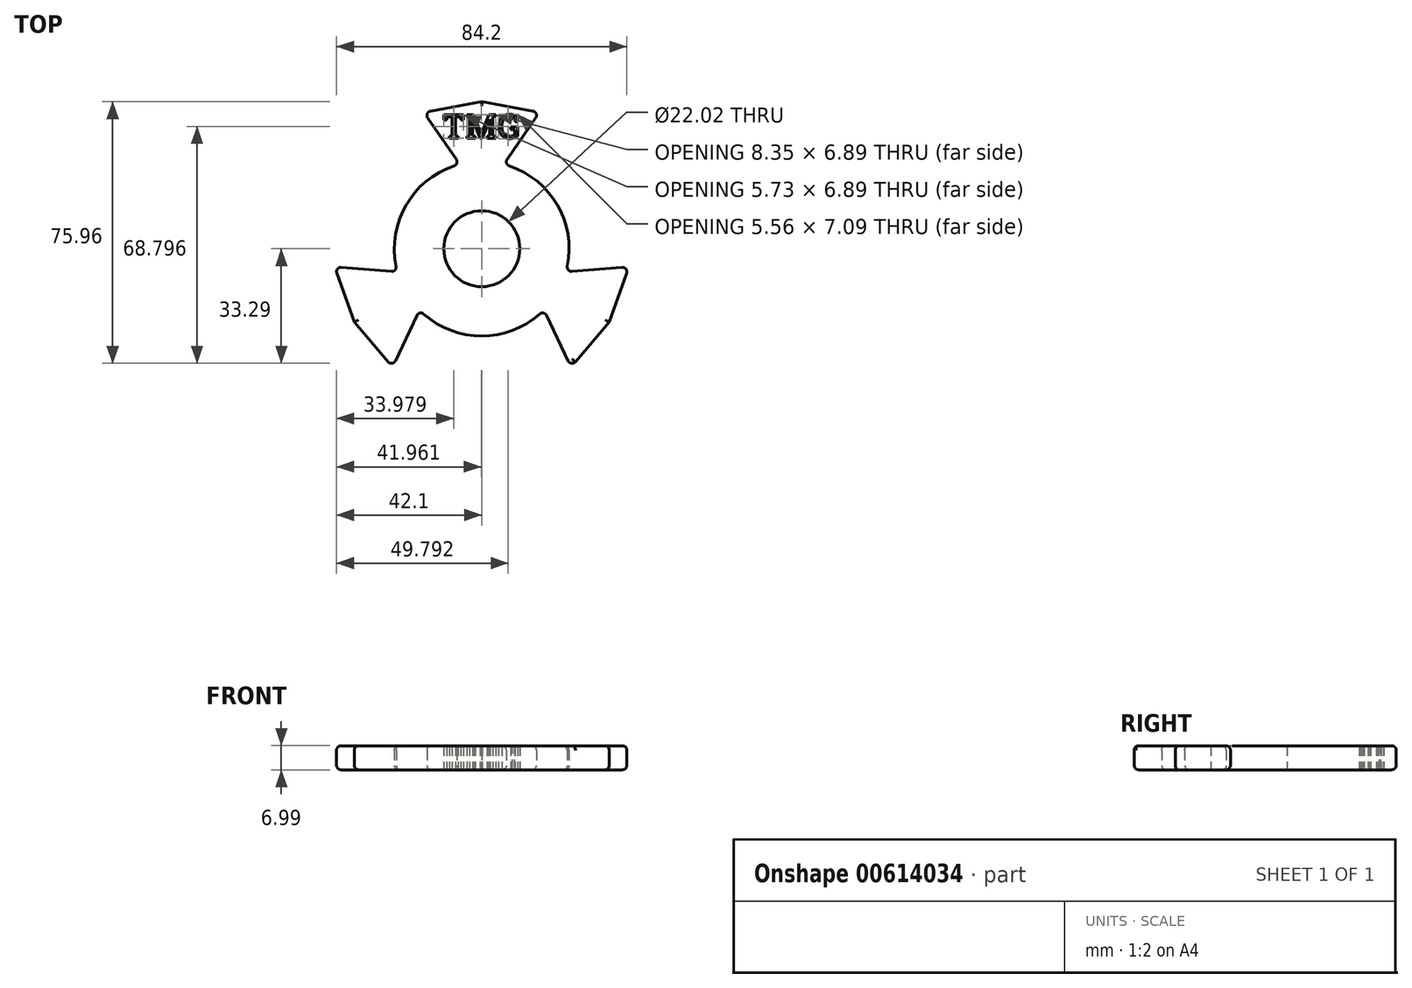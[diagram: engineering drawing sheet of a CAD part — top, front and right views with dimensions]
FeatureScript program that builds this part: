
annotation { "Feature Type Name" : "Feature", "Feature Type Description" : "" }
export const myFeature = defineFeature(function(context is Context, id is Id, definition is map)
    precondition{}
    {
        {
            var Q0;
            Q0=qCreatedBy(makeId("Top.planeOp"),FACE);
            var sketch = newSketch(context, id + "F0", { "sketchPlane" : qUnion([Q0])});
            skCircle(sketch, "E0", {"center": v(0, 0) * mm, "radius": 11.01 * mm});
            skCircle(sketch, "E1", {"center": v(0, 0) * mm, "radius": 25.34 * mm});
            skLineSegment(sketch, "E2", {"start": v(6.38, 24.52) * mm, "end": v(16.79, 39.6) * mm});
            skLineSegment(sketch, "E3", {"start": v(16.79, 39.6) * mm, "end": v(0, 42.67) * mm});
            skLineSegment(sketch, "E4", {"start": v(0, 42.67) * mm, "end": v(-16.79, 39.6) * mm});
            skLineSegment(sketch, "E5", {"start": v(-16.79, 39.6) * mm, "end": v(-6.38, 24.52) * mm});
            skLineSegment(sketch, "E6", {"start": v(-24.43, -6.73) * mm, "end": v(-42.68, -5.26) * mm});
            skLineSegment(sketch, "E7", {"start": v(-42.68, -5.26) * mm, "end": v(-36.96, -21.34) * mm});
            skLineSegment(sketch, "E8", {"start": v(-36.96, -21.34) * mm, "end": v(-25.9, -34.34) * mm});
            skLineSegment(sketch, "E9", {"start": v(-25.9, -34.34) * mm, "end": v(-18.04, -17.79) * mm});
            skLineSegment(sketch, "E10", {"start": v(18.04, -17.79) * mm, "end": v(25.9, -34.34) * mm});
            skLineSegment(sketch, "E11", {"start": v(25.9, -34.34) * mm, "end": v(36.96, -21.34) * mm});
            skLineSegment(sketch, "E12", {"start": v(36.96, -21.34) * mm, "end": v(42.68, -5.26) * mm});
            skLineSegment(sketch, "E13", {"start": v(42.68, -5.26) * mm, "end": v(24.43, -6.73) * mm});
            skLineSegment(sketch, "E14", {"start": v(0, 42.67) * mm, "end": v(0, 0) * mm});
            skLineSegment(sketch, "E15", {"start": v(-36.96, -21.34) * mm, "end": v(0, 0) * mm});
            skLineSegment(sketch, "E16", {"start": v(0, 0) * mm, "end": v(36.96, -21.34) * mm});
            skLineSegment(sketch, "E17", {"start": v(-24.43, -6.73) * mm, "end": v(-18.04, -17.79) * mm});
            skPoint(sketch, "E18", {"position": v(-21.24, -12.26) * mm});
            skLineSegment(sketch, "E19", {"start": v(18.04, -17.79) * mm, "end": v(24.43, -6.73) * mm});
            skLineSegment(sketch, "E20", {"start": v(-6.38, 24.52) * mm, "end": v(6.38, 24.52) * mm});
            skPoint(sketch, "E21", {"position": v(21.24, -12.26) * mm});
            skText(sketch, "E22", { "text": "T", "fontName": "RobotoSlab-Regular.ttf"});
            skText(sketch, "E23", { "text": "G", "fontName": "RobotoSlab-Regular.ttf"});
            skText(sketch, "E24", { "text": "M", "fontName": "RobotoSlab-Regular.ttf"});
            skPoint(sketch, "E25", {"position": v(-11.59, 32.06) * mm});
            skPoint(sketch, "E26", {"position": v(32.8, -6.06) * mm});
            skLineSegment(sketch, "E27.0", {"start": v(32.8, -6.06) * mm, "end": v(32.8, -6.06) * mm});
            skPoint(sketch, "E28", {"position": v(-21.64, -25.38) * mm});
            skLineSegment(sketch, "E29.0", {"start": v(-21.64, -25.38) * mm, "end": v(-21.64, -25.38) * mm});
            const initialGuessF0  = {"E22": [-0.01116, 0.03206, 1, 0, 0.00698], "E23": [0.00465, 0.03206, 1, 0, 0.00698], "E24": [-0.00465, 0.03206, 1, 0, 0.00698]};
            skSetInitialGuess(sketch, initialGuessF0);
            skSolve(sketch);
        }
        {
            var Q0;
            {var subQ1=sQuery(id+"F0.wireOp",EDGE,"E1");var subQ3=sQuery(id+"F0.wireOp",EDGE,"E16");var subQ4=makeQuery(id+"F0.imprint","INTERSECT",VERTEX,{"derivedFrom":[subQ1,subQ3]});Q0=makeQuery(id+"F0.imprint","IMPRINT",FACE,{"disambiguationData":[TD([[makeQuery(id+"F0.imprint","IMPRINT",EDGE,{"disambiguationData":[TD([[subQ4,1.0]])],"derivedFrom":subQ3}),-1.0]])]});}
            var Q1;
            {var subQ1=sQuery(id+"F0.wireOp",EDGE,"E24.sketch_text.stroke-4");Q1=makeQuery(id+"F0.imprint","IMPRINT",FACE,{"disambiguationData":[TD([[makeQuery(id+"F0.imprint","IMPRINT",EDGE,{"derivedFrom":subQ1}),1.0]])]});}
            var Q2;
            Q2 = qSketchRegion(id + "F0", true);
            var Q3;
            Q3=sQuery(id+"F0.wireOp",EDGE,"E6");
            var Q4;
            Q4=sQuery(id+"F0.wireOp",EDGE,"E7");
            var Q5;
            Q5=sQuery(id+"F0.wireOp",EDGE,"E8");
            var Q6;
            Q6=sQuery(id+"F0.wireOp",EDGE,"E9");
            var Q7;
            Q7=sQuery(id+"F0.wireOp",EDGE,"E5");
            var Q8;
            Q8=sQuery(id+"F0.wireOp",EDGE,"E4");
            var Q9;
            Q9=sQuery(id+"F0.wireOp",EDGE,"E3");
            var Q10;
            Q10=sQuery(id+"F0.wireOp",EDGE,"E2");
            var Q11;
            Q11=sQuery(id+"F0.wireOp",EDGE,"E1");
            extrude(context, id + "F1", {"entities" : qUnion([Q0, Q1, Q2]), "surfaceEntities" : qUnion([Q3, Q4, Q5, Q6, Q7, Q8, Q9, Q10, Q11]), "depth" : 7 * mm, "offsetDistance" : 25.4 * mm});
        }
        {
            var Q0;
            Q0=makeQuery(id+"F1.opExtrude","SWEPT_EDGE",EDGE,{"disambiguationData":[OSD([sQuery(id+"F0.wireOp",EDGE,"E4"),sQuery(id+"F0.wireOp",EDGE,"E5")])]});
            var Q1;
            Q1=makeQuery(id+"F1.opExtrude","SWEPT_EDGE",EDGE,{"disambiguationData":[OSD([sQuery(id+"F0.wireOp",EDGE,"E2"),sQuery(id+"F0.wireOp",EDGE,"E3")])]});
            var Q2;
            Q2=makeQuery(id+"F1.opExtrude","SWEPT_EDGE",EDGE,{"disambiguationData":[OSD([sQuery(id+"F0.wireOp",EDGE,"E1"),sQuery(id+"F0.wireOp",EDGE,"E5"),sQuery(id+"F0.wireOp",EDGE,"E20")])]});
            var Q3;
            Q3=makeQuery(id+"F1.opExtrude","SWEPT_EDGE",EDGE,{"disambiguationData":[OSD([sQuery(id+"F0.wireOp",EDGE,"E1"),sQuery(id+"F0.wireOp",EDGE,"E6"),sQuery(id+"F0.wireOp",EDGE,"E17")])]});
            var Q4;
            Q4=makeQuery(id+"F1.opExtrude","SWEPT_EDGE",EDGE,{"disambiguationData":[OSD([sQuery(id+"F0.wireOp",EDGE,"E6"),sQuery(id+"F0.wireOp",EDGE,"E7")])]});
            var Q5;
            Q5=makeQuery(id+"F1.opExtrude","SWEPT_EDGE",EDGE,{"disambiguationData":[OSD([sQuery(id+"F0.wireOp",EDGE,"E8"),sQuery(id+"F0.wireOp",EDGE,"E9")])]});
            var Q6;
            Q6=makeQuery(id+"F1.opExtrude","SWEPT_EDGE",EDGE,{"disambiguationData":[OSD([sQuery(id+"F0.wireOp",EDGE,"E1"),sQuery(id+"F0.wireOp",EDGE,"E9"),sQuery(id+"F0.wireOp",EDGE,"E17")])]});
            var Q7;
            Q7=makeQuery(id+"F1.opExtrude","SWEPT_EDGE",EDGE,{"disambiguationData":[OSD([sQuery(id+"F0.wireOp",EDGE,"E1"),sQuery(id+"F0.wireOp",EDGE,"E10"),sQuery(id+"F0.wireOp",EDGE,"E19")])]});
            var Q8;
            Q8=makeQuery(id+"F1.opExtrude","SWEPT_EDGE",EDGE,{"disambiguationData":[OSD([sQuery(id+"F0.wireOp",EDGE,"E10"),sQuery(id+"F0.wireOp",EDGE,"E11")])]});
            var Q9;
            Q9=makeQuery(id+"F1.opExtrude","SWEPT_EDGE",EDGE,{"disambiguationData":[OSD([sQuery(id+"F0.wireOp",EDGE,"E12"),sQuery(id+"F0.wireOp",EDGE,"E13")])]});
            var Q10;
            Q10=makeQuery(id+"F1.opExtrude","SWEPT_EDGE",EDGE,{"disambiguationData":[OSD([sQuery(id+"F0.wireOp",EDGE,"E1"),sQuery(id+"F0.wireOp",EDGE,"E13"),sQuery(id+"F0.wireOp",EDGE,"E19")])]});
            var Q11;
            Q11=makeQuery(id+"F1.opExtrude","SWEPT_EDGE",EDGE,{"disambiguationData":[OSD([sQuery(id+"F0.wireOp",EDGE,"E1"),sQuery(id+"F0.wireOp",EDGE,"E2"),sQuery(id+"F0.wireOp",EDGE,"E20")])]});
            fillet(context, id + "F2", {"entities" : qUnion([Q0, Q1, Q2, Q3, Q4, Q5, Q6, Q7, Q8, Q9, Q10, Q11]), "radius" : 1.27 * mm, "tangentPropagation" : true, "allowEdgeOverflow" : false});
        }
        {
            var Q0;
            Q0=makeQuery(id+"F1.opExtrude","CAP_EDGE",EDGE,{"disambiguationData":[OSD([sQuery(id+"F0.wireOp",EDGE,"E3")])],"isStart":false});
            var Q1;
            Q1=makeQuery(id+"F1.opExtrude","CAP_EDGE",EDGE,{"disambiguationData":[OSD([sQuery(id+"F0.wireOp",EDGE,"E2")])],"isStart":false});
            var Q2;
            Q2=makeQuery(id+"F1.opExtrude","CAP_EDGE",EDGE,{"disambiguationData":[OSD([sQuery(id+"F0.wireOp",EDGE,"E5")])],"isStart":false});
            var Q3;
            {var subQ0=sQuery(id+"F0.wireOp",EDGE,"E1");Q3=makeQuery(id+"F1.opExtrude","CAP_EDGE",EDGE,{"disambiguationData":[OSD([subQ0]),TDD([makeQuery(id+"F0.imprint","IMPRINT",EDGE,{"disambiguationData":[TD([[makeQuery(id+"F0.imprint","INTERSECT",VERTEX,{"derivedFrom":[subQ0,sQuery(id+"F0.wireOp",EDGE,"E9"),sQuery(id+"F0.wireOp",EDGE,"E17")]}),-1.0]])],"derivedFrom":subQ0})])],"isStart":false});}
            fillet(context, id + "F3", {"entities" : qUnion([Q0, Q1, Q2, Q3]), "radius" : 1.27 * mm, "tangentPropagation" : true, "allowEdgeOverflow" : false});
        }
        {
            var Q0;
            Q0=makeQuery(id+"F1.opExtrude","CAP_EDGE",EDGE,{"disambiguationData":[OSD([sQuery(id+"F0.wireOp",EDGE,"E9")])],"isStart":true});
            var Q1;
            {var subQ0=sQuery(id+"F0.wireOp",EDGE,"E1");Q1=makeQuery(id+"F1.opExtrude","CAP_EDGE",EDGE,{"disambiguationData":[OSD([subQ0]),TDD([makeQuery(id+"F0.imprint","IMPRINT",EDGE,{"disambiguationData":[TD([[makeQuery(id+"F0.imprint","INTERSECT",VERTEX,{"derivedFrom":[subQ0,sQuery(id+"F0.wireOp",EDGE,"E2"),sQuery(id+"F0.wireOp",EDGE,"E20")]}),1.0]])],"derivedFrom":subQ0})])],"isStart":true});}
            var Q2;
            {var subQ0=sQuery(id+"F0.wireOp",EDGE,"E1");Q2=makeQuery(id+"F1.opExtrude","CAP_EDGE",EDGE,{"disambiguationData":[OSD([subQ0]),TDD([makeQuery(id+"F0.imprint","IMPRINT",EDGE,{"disambiguationData":[TD([[makeQuery(id+"F0.imprint","INTERSECT",VERTEX,{"derivedFrom":[subQ0,sQuery(id+"F0.wireOp",EDGE,"E5"),sQuery(id+"F0.wireOp",EDGE,"E20")]}),-1.0]])],"derivedFrom":subQ0})])],"isStart":true});}
            fillet(context, id + "F4", {"entities" : qUnion([Q0, Q1, Q2]), "radius" : 1.27 * mm, "tangentPropagation" : true, "allowEdgeOverflow" : false});
        }
    });
